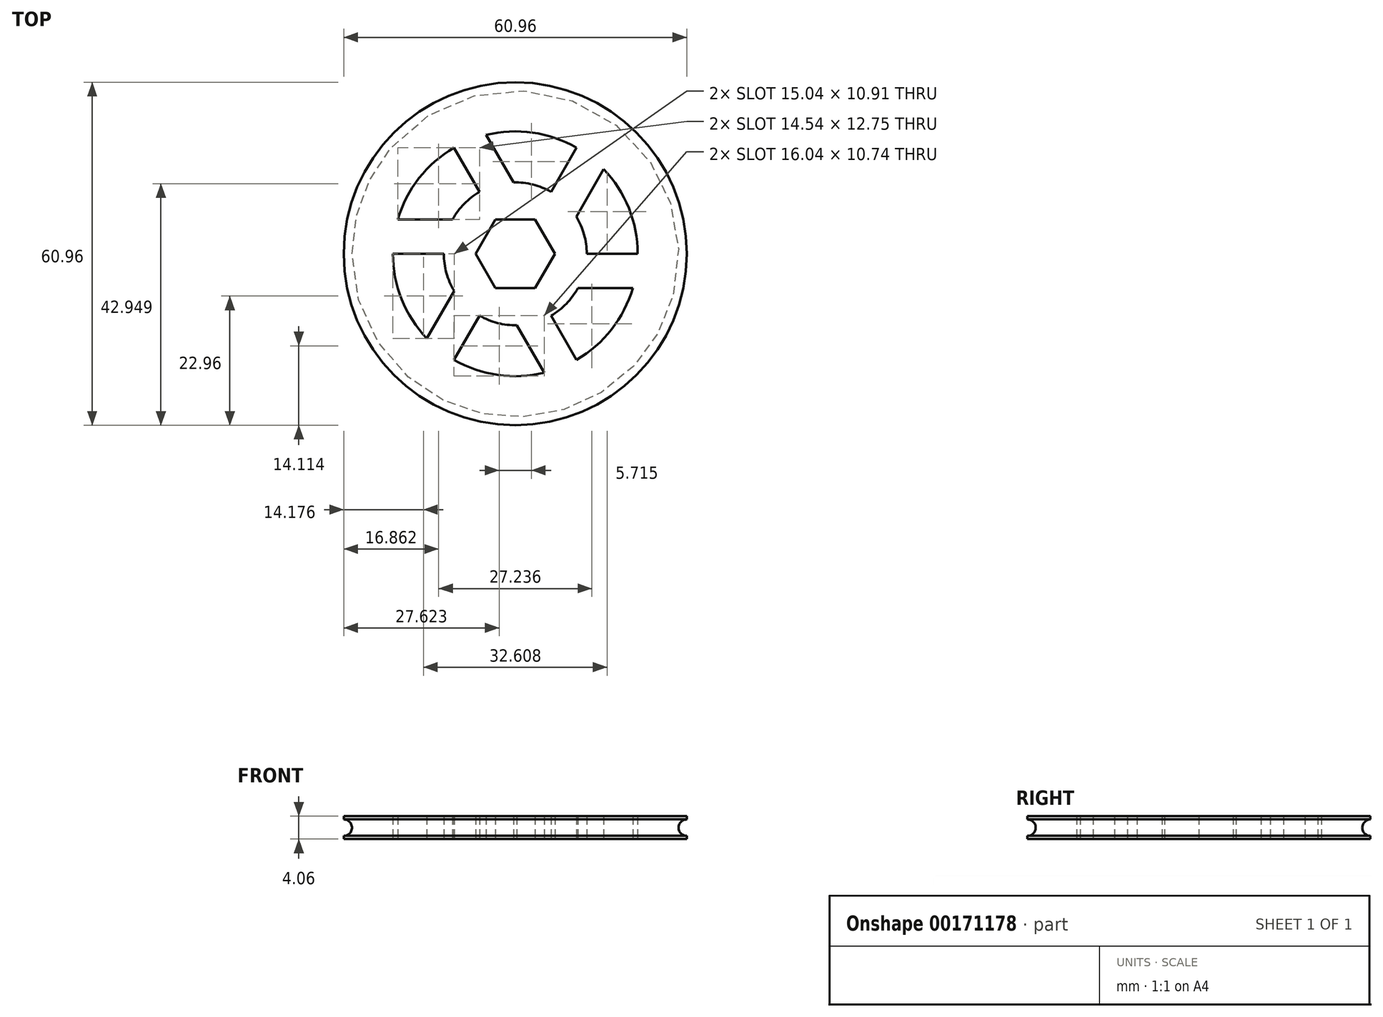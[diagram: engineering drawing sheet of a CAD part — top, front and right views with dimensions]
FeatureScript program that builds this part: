
annotation { "Feature Type Name" : "Feature", "Feature Type Description" : "" }
export const myFeature = defineFeature(function(context is Context, id is Id, definition is map)
    precondition{}
    {
        {
            var Q0;
            Q0=qCreatedBy(makeId("Top.planeOp"),FACE);
            var sketch = newSketch(context, id + "F0", { "sketchPlane" : qUnion([Q0])});
            skCircle(sketch, "E0.cCircle", {"center": v(0, 0) * mm, "radius": 6.1 * mm, "construction": true});
            skLineSegment(sketch, "E0.0", {"start": v(3.52, -6.1) * mm, "end": v(-3.52, -6.1) * mm});
            skLineSegment(sketch, "E0.1", {"start": v(-3.52, -6.1) * mm, "end": v(-7.04, 0) * mm});
            skLineSegment(sketch, "E0.2", {"start": v(-7.04, 0) * mm, "end": v(-3.52, 6.1) * mm});
            skLineSegment(sketch, "E0.3", {"start": v(-3.52, 6.1) * mm, "end": v(3.52, 6.1) * mm});
            skLineSegment(sketch, "E0.4", {"start": v(3.52, 6.1) * mm, "end": v(7.04, 0) * mm});
            skLineSegment(sketch, "E0.5", {"start": v(7.04, 0) * mm, "end": v(3.52, -6.1) * mm});
            skPoint(sketch, "E0.0.midPoint", {"position": v(0, -6.1) * mm});
            skArc(sketch, "E1", {"start": v(-12.7, 0) * mm, "mid": v(-12.23, -3.43) * mm, "end": v(-10.85, -6.6) * mm});
            skCircle(sketch, "E2", {"center": v(0, 0) * mm, "radius": 30.48 * mm});
            skArc(sketch, "E3", {"start": v(-21.76, 0) * mm, "mid": v(-20.2, -8.1) * mm, "end": v(-15.72, -15.04) * mm});
            skLineSegment(sketch, "E4", {"start": v(6.35, 11) * mm, "end": v(10.88, 18.84) * mm});
            skLineSegment(sketch, "E5", {"start": v(3.52, -6.1) * mm, "end": v(7.04, 0) * mm});
            skLineSegment(sketch, "E6", {"start": v(-7.04, 0) * mm, "end": v(-3.52, -6.1) * mm});
            skLineSegment(sketch, "E7", {"start": v(3.52, 6.1) * mm, "end": v(-3.52, 6.1) * mm});
            skPoint(sketch, "E7.endSnap0", {"position": v(0, 6.1) * mm});
            skLineSegment(sketch, "E8", {"start": v(-12.7, 0) * mm, "end": v(-21.76, 0) * mm});
            skLineSegment(sketch, "E9.trimOffspring", {"start": v(-11.14, 6.1) * mm, "end": v(-20.89, 6.1) * mm});
            skLineSegment(sketch, "E10.trimOffspring", {"start": v(10.85, 6.6) * mm, "end": v(15.72, 15.04) * mm});
            skArc(sketch, "E11.trimOffspring", {"start": v(6.35, 11) * mm, "mid": v(3.15, 12.3) * mm, "end": v(-0.3, 12.7) * mm});
            skArc(sketch, "E12.trimOffspring", {"start": v(10.88, 18.84) * mm, "mid": v(3.08, 21.54) * mm, "end": v(-5.16, 21.14) * mm});
            skLineSegment(sketch, "E13.trimOffspring", {"start": v(0.3, -12.7) * mm, "end": v(5.16, -21.14) * mm});
            skLineSegment(sketch, "E14", {"start": v(6.35, -11) * mm, "end": v(10.88, -18.84) * mm});
            skArc(sketch, "E15.trimOffspring", {"start": v(6.35, -11) * mm, "mid": v(9.08, -8.88) * mm, "end": v(11.14, -6.1) * mm});
            skArc(sketch, "E16.trimOffspring", {"start": v(10.88, -18.84) * mm, "mid": v(17.11, -13.44) * mm, "end": v(20.89, -6.1) * mm});
            skLineSegment(sketch, "E17", {"start": v(-10.85, -6.6) * mm, "end": v(-15.72, -15.04) * mm});
            skLineSegment(sketch, "E18", {"start": v(-6.35, -11) * mm, "end": v(-10.88, -18.84) * mm});
            skLineSegment(sketch, "E19", {"start": v(11.14, -6.1) * mm, "end": v(20.89, -6.1) * mm});
            skLineSegment(sketch, "E20", {"start": v(12.7, 0) * mm, "end": v(21.76, 0) * mm});
            skLineSegment(sketch, "E21", {"start": v(-0.3, 12.7) * mm, "end": v(-5.16, 21.14) * mm});
            skLineSegment(sketch, "E22", {"start": v(-6.35, 11) * mm, "end": v(-10.88, 18.84) * mm});
            skArc(sketch, "E23.trimOffspring", {"start": v(-10.88, 18.84) * mm, "mid": v(-17.11, 13.44) * mm, "end": v(-20.89, 6.1) * mm});
            skArc(sketch, "E24.trimOffspring", {"start": v(-6.35, 11) * mm, "mid": v(-9.08, 8.88) * mm, "end": v(-11.14, 6.1) * mm});
            skArc(sketch, "E25.trimOffspring", {"start": v(-6.35, -11) * mm, "mid": v(-3.15, -12.3) * mm, "end": v(0.3, -12.7) * mm});
            skArc(sketch, "E26.trimOffspring", {"start": v(-10.88, -18.84) * mm, "mid": v(-3.08, -21.54) * mm, "end": v(5.16, -21.14) * mm});
            skArc(sketch, "E27.trimOffspring", {"start": v(12.7, 0) * mm, "mid": v(12.23, 3.43) * mm, "end": v(10.85, 6.6) * mm});
            skArc(sketch, "E28.trimOffspring", {"start": v(21.76, 0) * mm, "mid": v(20.2, 8.1) * mm, "end": v(15.72, 15.04) * mm});
            skSolve(sketch);
        }
        {
            var Q0;
            Q0=makeQuery(id+"F0.imprint","IMPRINT",FACE,{"disambiguationData":[TD([[makeQuery(id+"F0.imprint","IMPRINT",EDGE,{"derivedFrom":sQuery(id+"F0.wireOp",EDGE,"E0.0")}),1.0]])]});
            extrude(context, id + "F1", {"entities" : qUnion([Q0]), "depth" : 4.06 * mm});
        }
        {
            var Q0;
            Q0=qCreatedBy(makeId("Right.planeOp"),FACE);
            var sketch = newSketch(context, id + "F2", { "sketchPlane" : qUnion([Q0])});
            skCircle(sketch, "E29", {"center": v(30.48, 2.03) * mm, "radius": 1.46 * mm});
            skSolve(sketch);
        }
        {
            var Q0;
            Q0=makeQuery(id+"F2.imprint","IMPRINT",FACE,{"disambiguationData":[TD([[makeQuery(id+"F2.imprint","IMPRINT",EDGE,{"derivedFrom":sQuery(id+"F2.wireOp",EDGE,"E29")}),1.0]])]});
            var Q1;
            Q1=sQuery(id+"F2.wireOp",EDGE,"E29");
            var Q2;
            Q2=makeQuery(id+"F1.opExtrude","SWEPT_FACE",FACE,{"disambiguationData":[OSD([sQuery(id+"F0.wireOp",EDGE,"E2")])]});
            revolve(context, id + "F3", {"operationType" : NewBodyOperationType.REMOVE, "entities" : qUnion([Q0]), "surfaceEntities" : qUnion([Q1]), "axis" : qUnion([Q2]), "revolveType" : RevolveType.FULL, "oppositeDirection" : true});
        }
    });
